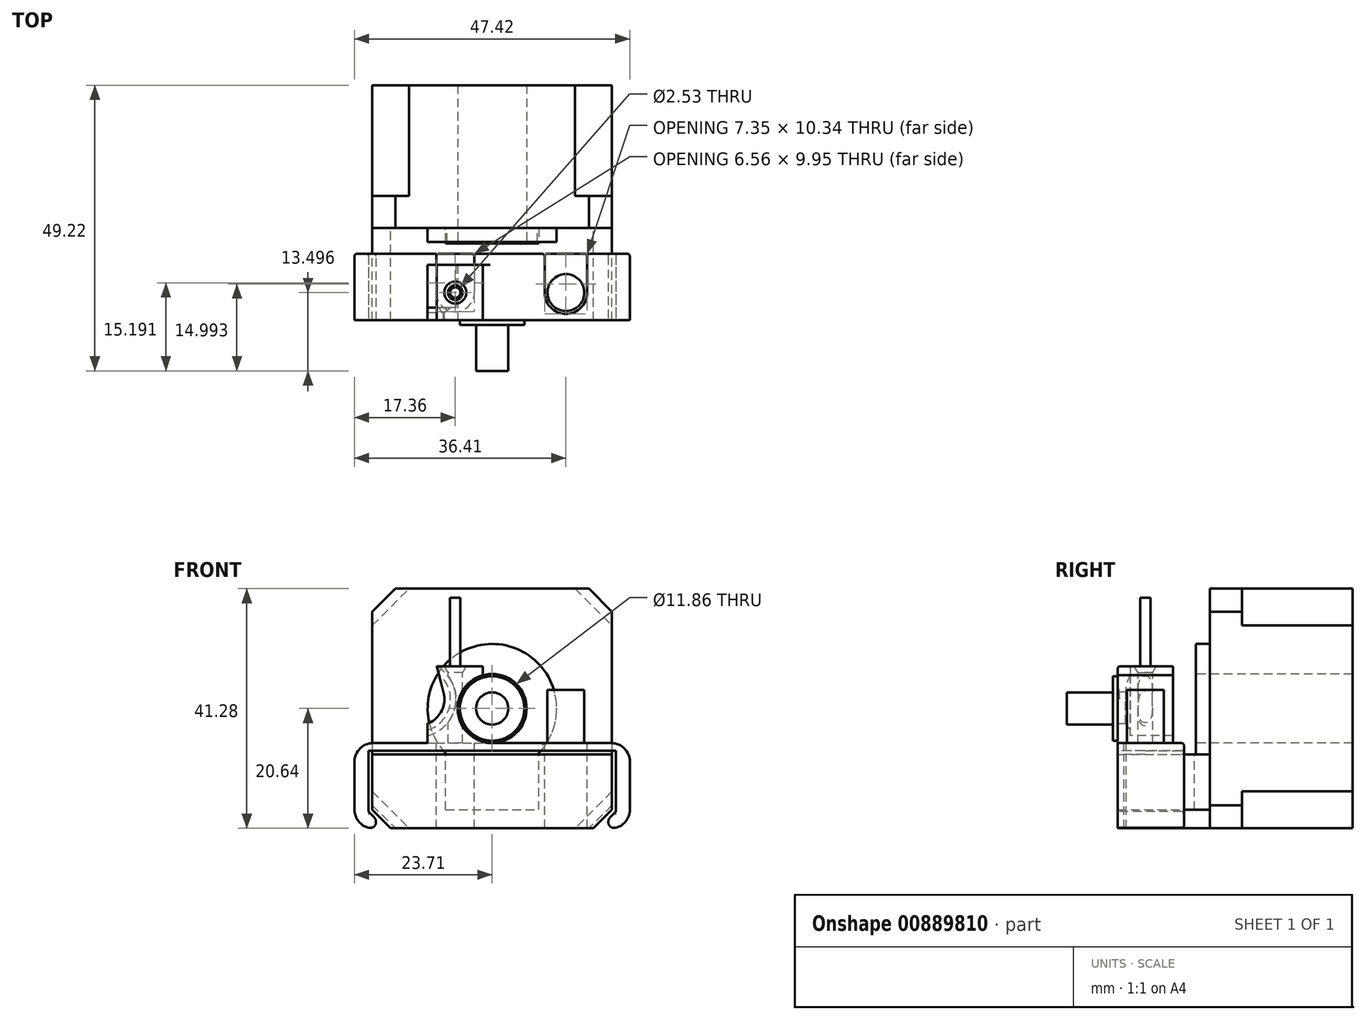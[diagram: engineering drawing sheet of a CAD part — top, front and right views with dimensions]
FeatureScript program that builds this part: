
annotation { "Feature Type Name" : "Feature", "Feature Type Description" : "" }
export const myFeature = defineFeature(function(context is Context, id is Id, definition is map)
    precondition{}
    {
        {
            var Q0;
            Q0=qCreatedBy(makeId("Front.planeOp"),FACE);
            var sketch = newSketch(context, id + "F0", { "sketchPlane" : qUnion([Q0])});
            skLineSegment(sketch, "E0.bottom", {"start": v(14.29, 20.64) * mm, "end": v(-14.29, 20.64) * mm});
            skLineSegment(sketch, "E0.top", {"start": v(14.29, -20.64) * mm, "end": v(-14.29, -20.64) * mm});
            skLineSegment(sketch, "E0.left", {"start": v(20.64, 14.29) * mm, "end": v(20.64, -14.29) * mm});
            skLineSegment(sketch, "E0.right", {"start": v(-20.64, 14.29) * mm, "end": v(-20.64, -14.29) * mm});
            skPoint(sketch, "E0.middle", {"position": v(0, 0) * mm});
            skLineSegment(sketch, "E1", {"start": v(-20.64, 14.29) * mm, "end": v(-14.29, 20.64) * mm});
            skLineSegment(sketch, "E2", {"start": v(14.29, 20.64) * mm, "end": v(20.64, 14.29) * mm});
            skLineSegment(sketch, "E3", {"start": v(20.64, -14.29) * mm, "end": v(14.29, -20.64) * mm});
            skLineSegment(sketch, "E4", {"start": v(-20.64, -14.29) * mm, "end": v(-14.29, -20.64) * mm});
            skPoint(sketch, "E5.orphan", {"position": v(20.64, -20.64) * mm});
            skPoint(sketch, "E6.orphan", {"position": v(20.64, 20.64) * mm});
            skPoint(sketch, "E7.orphan", {"position": v(-20.64, 20.64) * mm});
            skPoint(sketch, "E8.orphan", {"position": v(-20.64, -20.64) * mm});
            skSolve(sketch);
        }
        {
            var Q0;
            Q0=makeQuery(id+"F0.imprint","IMPRINT",FACE,{"disambiguationData":[TD([[makeQuery(id+"F0.imprint","IMPRINT",EDGE,{"derivedFrom":sQuery(id+"F0.wireOp",EDGE,"E0.bottom")}),1.0]])]});
            extrude(context, id + "F1", {"entities" : qUnion([Q0]), "endBound" : BoundingType.SYMMETRIC, "depth" : 19.05 * mm, "offsetDistance" : 25.4 * mm});
        }
        {
            var Q0;
            Q0=makeQuery(id+"F1.opExtrude","CAP_FACE",FACE,{"disambiguationData":[OSD([sQuery(id+"F0.wireOp",EDGE,"E0.bottom"),sQuery(id+"F0.wireOp",EDGE,"E0.top"),sQuery(id+"F0.wireOp",EDGE,"E0.left"),sQuery(id+"F0.wireOp",EDGE,"E0.right"),sQuery(id+"F0.wireOp",EDGE,"E1"),sQuery(id+"F0.wireOp",EDGE,"E2"),sQuery(id+"F0.wireOp",EDGE,"E3"),sQuery(id+"F0.wireOp",EDGE,"E4")])],"isStart":false});
            var sketch = newSketch(context, id + "F2", { "sketchPlane" : qUnion([Q0])});
            skLineSegment(sketch, "E9.bottom", {"start": v(-20.64, 20.64) * mm, "end": v(20.64, 20.64) * mm});
            skLineSegment(sketch, "E9.top", {"start": v(-20.64, -20.64) * mm, "end": v(20.64, -20.64) * mm});
            skLineSegment(sketch, "E9.left", {"start": v(-20.64, 20.64) * mm, "end": v(-20.64, -20.64) * mm});
            skLineSegment(sketch, "E9.right", {"start": v(20.64, 20.64) * mm, "end": v(20.64, -20.64) * mm});
            skPoint(sketch, "E9.middle", {"position": v(0, 0) * mm});
            skLineSegment(sketch, "E10", {"start": v(-20.64, 16.67) * mm, "end": v(-16.67, 20.64) * mm});
            skLineSegment(sketch, "E11", {"start": v(16.67, 20.64) * mm, "end": v(20.64, 16.67) * mm});
            skLineSegment(sketch, "E12", {"start": v(20.64, -16.67) * mm, "end": v(16.67, -20.64) * mm});
            skLineSegment(sketch, "E13", {"start": v(-20.64, -16.67) * mm, "end": v(-16.67, -20.64) * mm});
            skSolve(sketch);
        }
        {
            var Q0;
            {var subQ2=sQuery(id+"F2.wireOp",EDGE,"E10");Q0=makeQuery(id+"F2.imprint","IMPRINT",FACE,{"disambiguationData":[TD([[makeQuery(id+"F2.imprint","IMPRINT",EDGE,{"derivedFrom":subQ2}),-1.0]])]});}
            var Q1;
            {var subQ4=makeQuery(id+"F1.opExtrude","CAP_EDGE",EDGE,{"disambiguationData":[OSD([sQuery(id+"F0.wireOp",EDGE,"E1")])],"isStart":false});Q1=makeQuery(id+"F2.imprint","IMPRINT",FACE,{"disambiguationData":[TD([[makeQuery(id+"F2.imprint","IMPRINT",EDGE,{"derivedFrom":subQ4}),-1.0]])]});}
            var Q2;
            {var subQ2=sQuery(id+"F2.wireOp",EDGE,"E13");Q2=makeQuery(id+"F2.imprint","IMPRINT",FACE,{"disambiguationData":[TD([[makeQuery(id+"F2.imprint","IMPRINT",EDGE,{"derivedFrom":subQ2}),1.0]])]});}
            var Q3;
            {var subQ2=sQuery(id+"F2.wireOp",EDGE,"E12");Q3=makeQuery(id+"F2.imprint","IMPRINT",FACE,{"disambiguationData":[TD([[makeQuery(id+"F2.imprint","IMPRINT",EDGE,{"derivedFrom":subQ2}),-1.0]])]});}
            var Q4;
            {var subQ2=sQuery(id+"F2.wireOp",EDGE,"E11");Q4=makeQuery(id+"F2.imprint","IMPRINT",FACE,{"disambiguationData":[TD([[makeQuery(id+"F2.imprint","IMPRINT",EDGE,{"derivedFrom":subQ2}),-1.0]])]});}
            extrude(context, id + "F3", {"entities" : qUnion([Q0, Q1, Q2, Q3, Q4]), "operationType" : NewBodyOperationType.ADD, "depth" : 5.56 * mm, "offsetDistance" : 25.4 * mm});
        }
        {
            var Q0;
            Q0=makeQuery(id+"F3.opExtrude","CAP_FACE",FACE,{"disambiguationData":[OSD([sQuery(id+"F2.wireOp",EDGE,"E9.bottom"),sQuery(id+"F2.wireOp",EDGE,"E9.top"),sQuery(id+"F2.wireOp",EDGE,"E9.left"),sQuery(id+"F2.wireOp",EDGE,"E9.right"),sQuery(id+"F2.wireOp",EDGE,"E10"),sQuery(id+"F2.wireOp",EDGE,"E11"),sQuery(id+"F2.wireOp",EDGE,"E12"),sQuery(id+"F2.wireOp",EDGE,"E13")])],"isStart":false});
            var sketch = newSketch(context, id + "F4", { "sketchPlane" : qUnion([Q0])});
            skCircle(sketch, "E14", {"center": v(0, 0) * mm, "radius": 11.11 * mm});
            skSolve(sketch);
        }
        {
            var Q0;
            Q0=makeQuery(id+"F4.imprint","IMPRINT",FACE,{"disambiguationData":[TD([[makeQuery(id+"F4.imprint","IMPRINT",EDGE,{"derivedFrom":sQuery(id+"F4.wireOp",EDGE,"E14")}),1.0]])]});
            extrude(context, id + "F5", {"entities" : qUnion([Q0]), "operationType" : NewBodyOperationType.ADD, "depth" : 2.38 * mm, "offsetDistance" : 25.4 * mm});
        }
        {
            var Q0;
            Q0=makeQuery(id+"F5.opExtrude","CAP_FACE",FACE,{"disambiguationData":[OSD([sQuery(id+"F4.wireOp",EDGE,"E14")])],"isStart":false});
            var sketch = newSketch(context, id + "F6", { "sketchPlane" : qUnion([Q0])});
            skCircle(sketch, "E15", {"center": v(0, 0) * mm, "radius": 2.78 * mm});
            skSolve(sketch);
        }
        {
            var Q0;
            Q0=makeQuery(id+"F6.imprint","IMPRINT",FACE,{"disambiguationData":[TD([[makeQuery(id+"F6.imprint","IMPRINT",EDGE,{"derivedFrom":sQuery(id+"F6.wireOp",EDGE,"E15")}),1.0]])]});
            extrude(context, id + "F7", {"entities" : qUnion([Q0]), "operationType" : NewBodyOperationType.ADD, "depth" : 22.22 * mm, "offsetDistance" : 25.4 * mm});
        }
        {
            var Q0;
            Q0=makeQuery(id+"F5.opExtrude","CAP_FACE",FACE,{"disambiguationData":[OSD([sQuery(id+"F4.wireOp",EDGE,"E14")])],"isStart":false});
            cPlane(context, id + "F8", {"entities" : qUnion([Q0]), "cplaneType" : CPlaneType.OFFSET, "offset" : 4.76 * mm, "width" : 152.4 * mm, "height" : 152.4 * mm});
        }
        {
            var Q0;
            Q0=qCreatedBy(id+"F8.planeOp",FACE);
            var sketch = newSketch(context, id + "F9", { "sketchPlane" : qUnion([Q0])});
            skCircle(sketch, "E16", {"center": v(0, 0) * mm, "radius": 5.56 * mm});
            skSolve(sketch);
        }
        {
            var Q0;
            Q0=makeQuery(id+"F9.imprint","IMPRINT",FACE,{"disambiguationData":[TD([[makeQuery(id+"F9.imprint","IMPRINT",EDGE,{"derivedFrom":sQuery(id+"F9.wireOp",EDGE,"E16")}),1.0]])]});
            extrude(context, id + "F10", {"entities" : qUnion([Q0]), "operationType" : NewBodyOperationType.ADD, "depth" : 9.52 * mm, "offsetDistance" : 25.4 * mm});
        }
        {
            var Q0;
            Q0=makeQuery(id+"F3.opExtrude","CAP_FACE",FACE,{"disambiguationData":[OSD([sQuery(id+"F2.wireOp",EDGE,"E9.bottom"),sQuery(id+"F2.wireOp",EDGE,"E9.top"),sQuery(id+"F2.wireOp",EDGE,"E9.left"),sQuery(id+"F2.wireOp",EDGE,"E9.right"),sQuery(id+"F2.wireOp",EDGE,"E10"),sQuery(id+"F2.wireOp",EDGE,"E11"),sQuery(id+"F2.wireOp",EDGE,"E12"),sQuery(id+"F2.wireOp",EDGE,"E13")])],"isStart":false});
            var sketch = newSketch(context, id + "F11", { "sketchPlane" : qUnion([Q0])});
            skLineSegment(sketch, "E17.bottom", {"start": v(-17.46, -20.64) * mm, "end": v(17.46, -20.64) * mm});
            skLineSegment(sketch, "E17.top", {"start": v(-20.64, -7.94) * mm, "end": v(20.64, -7.94) * mm});
            skLineSegment(sketch, "E17.left", {"start": v(-20.64, -17.46) * mm, "end": v(-20.64, -7.94) * mm});
            skLineSegment(sketch, "E17.right", {"start": v(20.64, -17.46) * mm, "end": v(20.64, -7.94) * mm});
            skLineSegment(sketch, "E18", {"start": v(-20.64, -17.46) * mm, "end": v(-17.46, -20.64) * mm});
            skLineSegment(sketch, "E19", {"start": v(17.46, -20.64) * mm, "end": v(20.64, -17.46) * mm});
            skPoint(sketch, "E20.orphan", {"position": v(-20.64, -20.64) * mm});
            skSolve(sketch);
        }
        {
            var Q0;
            Q0 = qSketchRegion(id + "F11", true);
            extrude(context, id + "F12", {"entities" : qUnion([Q0]), "depth" : 15.88 * mm, "offsetDistance" : 25.4 * mm});
        }
        {
            var Q0;
            Q0=makeQuery(id+"F12.opExtrude","SWEPT_FACE",FACE,{"disambiguationData":[OSD([sQuery(id+"F11.wireOp",EDGE,"E17.top")])]});
            var sketch = newSketch(context, id + "F13", { "sketchPlane" : qUnion([Q0])});
            skLineSegment(sketch, "E21", {"start": v(-7.78, -17.46) * mm, "end": v(-7.78, -15.08) * mm});
            skLineSegment(sketch, "E22", {"start": v(7.78, -15.08) * mm, "end": v(7.78, -17.46) * mm});
            skLineSegment(sketch, "E23", {"start": v(-7.78, -17.46) * mm, "end": v(7.78, -17.46) * mm});
            skLineSegment(sketch, "E24.0", {"start": v(-8.03, -17.71) * mm, "end": v(-8.03, -15.08) * mm});
            skLineSegment(sketch, "E24.1", {"start": v(-8.03, -17.71) * mm, "end": v(8.03, -17.71) * mm});
            skLineSegment(sketch, "E24.2", {"start": v(8.03, -15.08) * mm, "end": v(8.03, -17.71) * mm});
            skLineSegment(sketch, "E25", {"start": v(-8.03, -15.08) * mm, "end": v(8.03, -15.08) * mm});
            skSolve(sketch);
        }
        {
            var Q0;
            {var subQ0=sQuery(id+"F13.wireOp",EDGE,"E21");Q0=makeQuery(id+"F13.imprint","IMPRINT",FACE,{"disambiguationData":[TD([[makeQuery(id+"F13.imprint","IMPRINT",EDGE,{"derivedFrom":subQ0}),-1.0]])]});}
            var Q1;
            {var subQ2=sQuery(id+"F13.wireOp",EDGE,"E21");Q1=makeQuery(id+"F13.imprint","IMPRINT",FACE,{"disambiguationData":[TD([[makeQuery(id+"F13.imprint","IMPRINT",EDGE,{"derivedFrom":subQ2}),1.0]])]});}
            extrude(context, id + "F14", {"entities" : qUnion([Q0, Q1]), "operationType" : NewBodyOperationType.REMOVE, "oppositeDirection" : true, "depth" : 9.52 * mm, "offsetDistance" : 25.4 * mm});
        }
        {
            var Q0;
            Q0=makeQuery(id+"F12.opExtrude","SWEPT_FACE",FACE,{"disambiguationData":[OSD([sQuery(id+"F11.wireOp",EDGE,"E17.top")])]});
            var sketch = newSketch(context, id + "F15", { "sketchPlane" : qUnion([Q0])});
            skCircle(sketch, "E26", {"center": v(-6.35, -26.2) * mm, "radius": 2.78 * mm});
            skSolve(sketch);
        }
        {
            var Q0;
            Q0=makeQuery(id+"F15.imprint","IMPRINT",FACE,{"disambiguationData":[TD([[makeQuery(id+"F15.imprint","IMPRINT",EDGE,{"derivedFrom":sQuery(id+"F15.wireOp",EDGE,"E26")}),1.0]])]});
            extrude(context, id + "F16", {"entities" : qUnion([Q0]), "operationType" : NewBodyOperationType.ADD, "depth" : 1.59 * mm, "offsetDistance" : 25.4 * mm});
        }
        {
            var Q0;
            Q0=makeQuery(id+"F12.opExtrude","SWEPT_FACE",FACE,{"disambiguationData":[OSD([sQuery(id+"F11.wireOp",EDGE,"E17.top")])]});
            var sketch = newSketch(context, id + "F17", { "sketchPlane" : qUnion([Q0])});
            skCircle(sketch, "E27", {"center": v(12.7, -26.2) * mm, "radius": 3.18 * mm});
            skSolve(sketch);
        }
        {
            var Q0;
            Q0=makeQuery(id+"F17.imprint","IMPRINT",FACE,{"disambiguationData":[TD([[makeQuery(id+"F17.imprint","IMPRINT",EDGE,{"derivedFrom":sQuery(id+"F17.wireOp",EDGE,"E27")}),1.0]])]});
            extrude(context, id + "F18", {"entities" : qUnion([Q0]), "operationType" : NewBodyOperationType.ADD, "depth" : 11.1 * mm, "offsetDistance" : 25.4 * mm});
        }
        {
            var Q0;
            Q0=makeQuery(id+"F16.opExtrude","CAP_FACE",FACE,{"disambiguationData":[OSD([sQuery(id+"F15.wireOp",EDGE,"E26")])],"isStart":false});
            var sketch = newSketch(context, id + "F19", { "sketchPlane" : qUnion([Q0])});
            skCircle(sketch, "E28", {"center": v(-6.35, -26.2) * mm, "radius": 0.89 * mm});
            skSolve(sketch);
        }
        {
            var Q0;
            Q0=makeQuery(id+"F19.imprint","IMPRINT",FACE,{"disambiguationData":[TD([[makeQuery(id+"F19.imprint","IMPRINT",EDGE,{"derivedFrom":sQuery(id+"F19.wireOp",EDGE,"E28")}),1.0]])]});
            extrude(context, id + "F20", {"entities" : qUnion([Q0]), "depth" : 25.4 * mm, "offsetDistance" : 25.4 * mm});
        }
        {
            var Q0;
            Q0=makeQuery(id+"F20.opExtrude","CAP_FACE",FACE,{"disambiguationData":[OSD([sQuery(id+"F19.wireOp",EDGE,"E28")])],"isStart":false});
            var sketch = newSketch(context, id + "F21", { "sketchPlane" : qUnion([Q0])});
            skPoint(sketch, "E29", {"position": v(-6.35, -26.2) * mm});
            skSolve(sketch);
        }
        {
            var Q0;
            Q0=sQuery(id+"F21.wireOp",VERTEX,"E29");
            var Q1;
            Q1=qCreatedBy(makeId("Front.planeOp"),FACE);
            cPlane(context, id + "F22", {"entities" : qUnion([Q0, Q1]), "cplaneType" : CPlaneType.PLANE_POINT, "offset" : 25.4 * mm, "width" : 152.4 * mm, "height" : 152.4 * mm});
        }
        {
            var Q0;
            Q0=qCreatedBy(id+"F22.planeOp",FACE);
            var sketch = newSketch(context, id + "F23", { "sketchPlane" : qUnion([Q0])});
            skCircle(sketch, "E30", {"center": v(-12.7, 1.59) * mm, "radius": 6.1 * mm});
            skSolve(sketch);
        }
        {
            var Q0;
            Q0=makeQuery(id+"F23.imprint","IMPRINT",FACE,{"disambiguationData":[TD([[makeQuery(id+"F23.imprint","IMPRINT",EDGE,{"derivedFrom":sQuery(id+"F23.wireOp",EDGE,"E30")}),1.0]])]});
            extrude(context, id + "F24", {"entities" : qUnion([Q0]), "endBound" : BoundingType.SYMMETRIC, "depth" : 3.17 * mm, "offsetDistance" : 25.4 * mm});
        }
        {
            var Q0;
            Q0=makeQuery(id+"F12.opExtrude","CAP_FACE",FACE,{"disambiguationData":[OSD([sQuery(id+"F11.wireOp",EDGE,"E17.bottom"),sQuery(id+"F11.wireOp",EDGE,"E17.top"),sQuery(id+"F11.wireOp",EDGE,"E17.left"),sQuery(id+"F11.wireOp",EDGE,"E17.right"),sQuery(id+"F11.wireOp",EDGE,"E18"),sQuery(id+"F11.wireOp",EDGE,"E19")])],"isStart":false});
            var sketch = newSketch(context, id + "F25", { "sketchPlane" : qUnion([Q0])});
            skLineSegment(sketch, "E31.0", {"start": v(21.33, -7.25) * mm, "end": v(-21.33, -7.25) * mm});
            skLineSegment(sketch, "E31.1", {"start": v(-21.33, -17.75) * mm, "end": v(-17.75, -21.33) * mm});
            skLineSegment(sketch, "E31.2", {"start": v(-17.75, -21.33) * mm, "end": v(17.75, -21.33) * mm});
            skLineSegment(sketch, "E31.3", {"start": v(-21.33, -7.25) * mm, "end": v(-21.33, -17.75) * mm});
            skLineSegment(sketch, "E31.4", {"start": v(17.75, -21.33) * mm, "end": v(21.33, -17.75) * mm});
            skLineSegment(sketch, "E31.5", {"start": v(21.33, -17.75) * mm, "end": v(21.33, -7.25) * mm});
            skLineSegment(sketch, "E32.bottom", {"start": v(-23.7, -20.64) * mm, "end": v(23.7, -20.64) * mm});
            skLineSegment(sketch, "E32.top", {"start": v(-23.7, -5.98) * mm, "end": v(23.7, -5.98) * mm});
            skLineSegment(sketch, "E32.left", {"start": v(-23.7, -20.64) * mm, "end": v(-23.7, -5.98) * mm});
            skLineSegment(sketch, "E32.right", {"start": v(23.7, -20.64) * mm, "end": v(23.7, -5.98) * mm});
            skPoint(sketch, "E32.middle", {"position": v(0, -13.3) * mm});
            skPoint(sketch, "E32.middle.positionSnap0", {"position": v(0, -20.64) * mm});
            skPoint(sketch, "E32.centerSnap0", {"position": v(0, -20.64) * mm});
            skLineSegment(sketch, "E33.0", {"start": v(-9.13, -6.35) * mm, "end": v(-3.57, -6.35) * mm, "construction": true});
            skSolve(sketch);
        }
        {
            var Q0;
            Q0=makeQuery(id+"F25.imprint","IMPRINT",FACE,{"disambiguationData":[TD([[makeQuery(id+"F25.imprint","IMPRINT",EDGE,{"derivedFrom":sQuery(id+"F25.wireOp",EDGE,"E31.0")}),-1.0]])]});
            var Q1;
            Q1=makeQuery(id+"F10.opExtrude","CAP_FACE",FACE,{"disambiguationData":[OSD([sQuery(id+"F9.wireOp",EDGE,"E16")])],"isStart":true});
            extrude(context, id + "F26", {"entities" : qUnion([Q0]), "oppositeDirection" : true, "depth" : 11.43 * mm, "endBoundEntityFace" : qUnion([Q1]), "offsetDistance" : 25.4 * mm});
        }
        {
            var Q0;
            Q0=makeQuery(id+"F26.opExtrude","SWEPT_FACE",FACE,{"disambiguationData":[OSD([sQuery(id+"F25.wireOp",EDGE,"E32.top")])]});
            var sketch = newSketch(context, id + "F27", { "sketchPlane" : qUnion([Q0])});
            skArc(sketch, "E34.0", {"start": v(-9.63, -26.2) * mm, "mid": v(-6.35, -29.47) * mm, "end": v(-3.07, -26.2) * mm});
            skArc(sketch, "E35.0", {"start": v(9.03, -26.2) * mm, "mid": v(12.7, -29.87) * mm, "end": v(16.38, -26.2) * mm});
            skCircle(sketch, "E36", {"center": v(12.7, -26.2) * mm, "radius": 3.18 * mm, "construction": true});
            skLineSegment(sketch, "E37", {"start": v(15.34, -27.95) * mm, "end": v(15.76, -28.23) * mm, "construction": true});
            skLineSegment(sketch, "E38", {"start": v(-8.09, -28.97) * mm, "end": v(-7.82, -28.55) * mm, "construction": true});
            skLineSegment(sketch, "E39", {"start": v(-9.63, -26.2) * mm, "end": v(-9.63, -19.53) * mm});
            skLineSegment(sketch, "E40", {"start": v(-3.07, -19.53) * mm, "end": v(-3.07, -26.2) * mm});
            skLineSegment(sketch, "E41", {"start": v(-9.63, -19.53) * mm, "end": v(-3.07, -19.53) * mm});
            skLineSegment(sketch, "E42", {"start": v(9.03, -26.2) * mm, "end": v(9.03, -19.53) * mm});
            skLineSegment(sketch, "E43", {"start": v(9.03, -19.53) * mm, "end": v(16.38, -19.53) * mm});
            skLineSegment(sketch, "E44", {"start": v(16.38, -19.53) * mm, "end": v(16.38, -26.2) * mm});
            skSolve(sketch);
        }
        {
            var Q0;
            Q0=makeQuery(id+"F27.imprint","IMPRINT",FACE,{"disambiguationData":[TD([[makeQuery(id+"F27.imprint","IMPRINT",EDGE,{"derivedFrom":sQuery(id+"F27.wireOp",EDGE,"E34.0")}),1.0]])]});
            var Q1;
            Q1=makeQuery(id+"F27.imprint","IMPRINT",FACE,{"disambiguationData":[TD([[makeQuery(id+"F27.imprint","IMPRINT",EDGE,{"derivedFrom":sQuery(id+"F27.wireOp",EDGE,"E35.0")}),1.0]])]});
            extrude(context, id + "F28", {"entities" : qUnion([Q0, Q1]), "operationType" : NewBodyOperationType.REMOVE, "endBound" : BoundingType.THROUGH_ALL, "oppositeDirection" : true, "depth" : 25.4 * mm, "offsetDistance" : 25.4 * mm});
        }
        {
            var Q0;
            Q0=makeQuery(id+"F26.opExtrude","SWEPT_FACE",FACE,{"disambiguationData":[OSD([sQuery(id+"F25.wireOp",EDGE,"E32.top")])]});
            var sketch = newSketch(context, id + "F29", { "sketchPlane" : qUnion([Q0])});
            skLineSegment(sketch, "E45.bottom", {"start": v(-11.11, -30.96) * mm, "end": v(-1.59, -30.96) * mm});
            skLineSegment(sketch, "E45.top", {"start": v(-11.11, -21.43) * mm, "end": v(-1.59, -21.43) * mm});
            skLineSegment(sketch, "E45.left", {"start": v(-11.11, -30.96) * mm, "end": v(-11.11, -21.43) * mm});
            skLineSegment(sketch, "E45.right", {"start": v(-1.59, -30.96) * mm, "end": v(-1.59, -21.43) * mm});
            skPoint(sketch, "E45.middle", {"position": v(-6.35, -26.2) * mm});
            skSolve(sketch);
        }
        {
            var Q0;
            Q0 = qSketchRegion(id + "F29", true);
            extrude(context, id + "F30", {"entities" : qUnion([Q0]), "operationType" : NewBodyOperationType.ADD, "depth" : 13.2 * mm, "offsetDistance" : 25.4 * mm});
        }
        {
            var Q0;
            Q0=makeQuery(id+"F24.opExtrude","CAP_FACE",FACE,{"disambiguationData":[OSD([sQuery(id+"F23.wireOp",EDGE,"E30")])],"isStart":false});
            cPlane(context, id + "F31", {"entities" : qUnion([Q0]), "cplaneType" : CPlaneType.OFFSET, "offset" : 1 * mm, "width" : 152.4 * mm, "height" : 152.4 * mm});
        }
        {
            var Q0;
            Q0=qCreatedBy(id+"F31.planeOp",FACE);
            var sketch = newSketch(context, id + "F32", { "sketchPlane" : qUnion([Q0])});
            skCircle(sketch, "E46.0", {"center": v(-12.7, 1.59) * mm, "radius": 6.47 * mm});
            skSolve(sketch);
        }
        {
            var Q0;
            Q0=makeQuery(id+"F32.imprint","IMPRINT",FACE,{"disambiguationData":[TD([[makeQuery(id+"F32.imprint","IMPRINT",EDGE,{"derivedFrom":sQuery(id+"F32.wireOp",EDGE,"E46.0")}),1.0]])]});
            var Q1;
            {var subQ0=sQuery(id+"F25.wireOp",EDGE,"E32.left");var subQ1=sQuery(id+"F25.wireOp",EDGE,"E32.bottom");var subQ2=sQuery(id+"F25.wireOp",EDGE,"E31.1");var subQ3=sQuery(id+"F25.wireOp",EDGE,"E31.3");var subQ4=sQuery(id+"F25.wireOp",EDGE,"E31.0");var subQ5=sQuery(id+"F25.wireOp",EDGE,"E32.top");Q1=makeQuery(id+"F28.boolean.opBoolean","SPLIT",FACE,{"disambiguationData":[TD([makeQuery(id+"F26.opExtrude","SWEPT_FACE",FACE,{"disambiguationData":[OSD([subQ2])]})])],"derivedFrom":makeQuery(id+"F26.opExtrude","CAP_FACE",FACE,{"disambiguationData":[OSD([subQ4,subQ2,subQ3,sQuery(id+"F25.wireOp",EDGE,"E31.4"),sQuery(id+"F25.wireOp",EDGE,"E31.5"),subQ1,subQ5,subQ0,sQuery(id+"F25.wireOp",EDGE,"E32.right")])],"isStart":false})});}
            extrude(context, id + "F33", {"entities" : qUnion([Q0]), "operationType" : NewBodyOperationType.REMOVE, "endBound" : BoundingType.UP_TO_SURFACE, "oppositeDirection" : true, "depth" : 25.4 * mm, "endBoundEntityFace" : qUnion([Q1]), "offsetDistance" : 25.4 * mm});
        }
        {
            var Q0;
            Q0=makeQuery(id+"F30.boolean.opBoolean","MERGE",FACE,{"derivedFrom":[makeQuery(id+"F26.opExtrude","CAP_FACE",FACE,{"disambiguationData":[OSD([sQuery(id+"F25.wireOp",EDGE,"E31.0"),sQuery(id+"F25.wireOp",EDGE,"E31.1"),sQuery(id+"F25.wireOp",EDGE,"E31.3"),sQuery(id+"F25.wireOp",EDGE,"E31.4"),sQuery(id+"F25.wireOp",EDGE,"E31.5"),sQuery(id+"F25.wireOp",EDGE,"E32.bottom"),sQuery(id+"F25.wireOp",EDGE,"E32.top"),sQuery(id+"F25.wireOp",EDGE,"E32.left"),sQuery(id+"F25.wireOp",EDGE,"E32.right")])],"isStart":true}),makeQuery(id+"F30.opExtrude","SWEPT_FACE",FACE,{"disambiguationData":[OSD([sQuery(id+"F29.wireOp",EDGE,"E45.bottom")])]})]});
            var sketch = newSketch(context, id + "F34", { "sketchPlane" : qUnion([Q0])});
            skCircle(sketch, "E47.0", {"center": v(0, 0) * mm, "radius": 5.93 * mm});
            skSolve(sketch);
        }
        {
            var Q0;
            Q0 = qSketchRegion(id + "F34", true);
            extrude(context, id + "F35", {"entities" : qUnion([Q0]), "operationType" : NewBodyOperationType.REMOVE, "endBound" : BoundingType.THROUGH_ALL, "oppositeDirection" : true, "depth" : 25.4 * mm, "offsetDistance" : 25.4 * mm});
        }
        {
            var Q0;
            Q0=makeQuery(id+"F30.opExtrude","CAP_FACE",FACE,{"disambiguationData":[OSD([sQuery(id+"F29.wireOp",EDGE,"E45.bottom"),sQuery(id+"F29.wireOp",EDGE,"E45.top"),sQuery(id+"F29.wireOp",EDGE,"E45.left"),sQuery(id+"F29.wireOp",EDGE,"E45.right")])],"isStart":false});
            var sketch = newSketch(context, id + "F36", { "sketchPlane" : qUnion([Q0])});
            skCircle(sketch, "E48.0", {"center": v(-6.35, -26.2) * mm, "radius": 1.26 * mm});
            skSolve(sketch);
        }
        {
            var Q0;
            Q0 = qSketchRegion(id + "F36", true);
            extrude(context, id + "F37", {"entities" : qUnion([Q0]), "operationType" : NewBodyOperationType.REMOVE, "endBound" : BoundingType.THROUGH_ALL, "oppositeDirection" : true, "depth" : 25.4 * mm, "offsetDistance" : 25.4 * mm});
        }
        {
            var Q0;
            Q0=makeQuery(id+"F30.opExtrude","CAP_EDGE",EDGE,{"disambiguationData":[OSD([sQuery(id+"F29.wireOp",EDGE,"E45.left")])],"isStart":true});
            var Q1;
            Q1=makeQuery(id+"F30.opExtrude","CAP_EDGE",EDGE,{"disambiguationData":[OSD([sQuery(id+"F29.wireOp",EDGE,"E45.right")])],"isStart":true});
            var Q2;
            Q2=makeQuery(id+"F26.opExtrude","SWEPT_EDGE",EDGE,{"disambiguationData":[OSD([sQuery(id+"F25.wireOp",EDGE,"E32.top"),sQuery(id+"F25.wireOp",EDGE,"E32.left")])]});
            var Q3;
            Q3=makeQuery(id+"F26.opExtrude","SWEPT_EDGE",EDGE,{"disambiguationData":[OSD([sQuery(id+"F25.wireOp",EDGE,"E32.bottom"),sQuery(id+"F25.wireOp",EDGE,"E32.left")])]});
            var Q4;
            Q4=makeQuery(id+"F26.opExtrude","SWEPT_EDGE",EDGE,{"disambiguationData":[OSD([sQuery(id+"F25.wireOp",EDGE,"E32.top"),sQuery(id+"F25.wireOp",EDGE,"E32.right")])]});
            var Q5;
            Q5=makeQuery(id+"F26.opExtrude","SWEPT_EDGE",EDGE,{"disambiguationData":[OSD([sQuery(id+"F25.wireOp",EDGE,"E32.bottom"),sQuery(id+"F25.wireOp",EDGE,"E32.right")])]});
            fillet(context, id + "F38", {"entities" : qUnion([Q0, Q1, Q2, Q3, Q4, Q5]), "radius" : 3.17 * mm, "tangentPropagation" : true, "allowEdgeOverflow" : false});
        }
        {
            var Q0;
            Q0=makeQuery(id+"F38.opFillet","BLEND_EDGE",EDGE,{"blendedFrom":[makeQuery(id+"F30.opExtrude","CAP_EDGE",EDGE,{"disambiguationData":[OSD([sQuery(id+"F29.wireOp",EDGE,"E45.left")])],"isStart":true}),makeQuery(id+"F33.boolean.opBoolean","COPY",FACE,{"derivedFrom":makeQuery(id+"F33.opExtrude","SWEPT_FACE",FACE,{"disambiguationData":[OSD([sQuery(id+"F32.wireOp",EDGE,"E46.0")])]})})],"blendedInto":[makeQuery(id+"F33.boolean.opBoolean","COPY",FACE,{"derivedFrom":makeQuery(id+"F33.opExtrude","SWEPT_FACE",FACE,{"disambiguationData":[OSD([sQuery(id+"F32.wireOp",EDGE,"E46.0")])]})})]});
            var Q1;
            Q1=makeQuery(id+"F38.opFillet","BLEND_EDGE",EDGE,{"blendedFrom":[makeQuery(id+"F30.opExtrude","CAP_EDGE",EDGE,{"disambiguationData":[OSD([sQuery(id+"F29.wireOp",EDGE,"E45.right")])],"isStart":true}),makeQuery(id+"F35.boolean.opBoolean","COPY",FACE,{"derivedFrom":makeQuery(id+"F35.opExtrude","SWEPT_FACE",FACE,{"disambiguationData":[OSD([sQuery(id+"F34.wireOp",EDGE,"E47.0")])]})})],"blendedInto":[makeQuery(id+"F35.boolean.opBoolean","COPY",FACE,{"derivedFrom":makeQuery(id+"F35.opExtrude","SWEPT_FACE",FACE,{"disambiguationData":[OSD([sQuery(id+"F34.wireOp",EDGE,"E47.0")])]})})]});
            var Q2;
            Q2=makeQuery(id+"F26.opExtrude","SWEPT_EDGE",EDGE,{"disambiguationData":[OSD([sQuery(id+"F25.wireOp",EDGE,"E31.1"),sQuery(id+"F25.wireOp",EDGE,"E32.bottom")])]});
            var Q3;
            Q3=makeQuery(id+"F26.opExtrude","SWEPT_EDGE",EDGE,{"disambiguationData":[OSD([sQuery(id+"F25.wireOp",EDGE,"E31.4"),sQuery(id+"F25.wireOp",EDGE,"E32.bottom")])]});
            fillet(context, id + "F39", {"entities" : qUnion([Q0, Q1, Q2, Q3]), "radius" : 1.27 * mm, "tangentPropagation" : true, "allowEdgeOverflow" : false});
        }
        {
            var Q0;
            {var subQ0=sQuery(id+"F25.wireOp",EDGE,"E32.bottom");Q0=makeQuery(id+"F39.opFillet","BLEND_EDGE",EDGE,{"blendedFrom":[makeQuery(id+"F26.opExtrude","SWEPT_EDGE",EDGE,{"disambiguationData":[OSD([sQuery(id+"F25.wireOp",EDGE,"E31.1"),subQ0])]}),makeQuery(id+"F38.opFillet","BLEND_FACE",FACE,{"disambiguationData":[OSD([subQ0,sQuery(id+"F25.wireOp",EDGE,"E32.left")])]})],"blendedInto":[makeQuery(id+"F38.opFillet","BLEND_FACE",FACE,{"disambiguationData":[OSD([subQ0,sQuery(id+"F25.wireOp",EDGE,"E32.left")])]})]});}
            var Q1;
            {var subQ0=sQuery(id+"F25.wireOp",EDGE,"E32.bottom");Q1=makeQuery(id+"F39.opFillet","BLEND_EDGE",EDGE,{"blendedFrom":[makeQuery(id+"F26.opExtrude","SWEPT_EDGE",EDGE,{"disambiguationData":[OSD([sQuery(id+"F25.wireOp",EDGE,"E31.4"),subQ0])]}),makeQuery(id+"F38.opFillet","BLEND_FACE",FACE,{"disambiguationData":[OSD([subQ0,sQuery(id+"F25.wireOp",EDGE,"E32.right")])]})],"blendedInto":[makeQuery(id+"F38.opFillet","BLEND_FACE",FACE,{"disambiguationData":[OSD([subQ0,sQuery(id+"F25.wireOp",EDGE,"E32.right")])]})]});}
            fillet(context, id + "F40", {"entities" : qUnion([Q0, Q1]), "radius" : 1.02 * mm, "tangentPropagation" : true, "allowEdgeOverflow" : false});
        }
        {
            var Q0;
            Q0=qCreatedBy(id+"F22.planeOp",FACE);
            var sketch = newSketch(context, id + "F41", { "sketchPlane" : qUnion([Q0])});
            skLineSegment(sketch, "E49", {"start": v(-5.09, 3.05) * mm, "end": v(-5.09, 7.23) * mm});
            skLineSegment(sketch, "E50", {"start": v(-7.62, 7.23) * mm, "end": v(-7.62, 5.59) * mm, "construction": true});
            skLineSegment(sketch, "E51", {"start": v(-7.62, -2.41) * mm, "end": v(-7.62, -5.98) * mm});
            skLineSegment(sketch, "E52", {"start": v(-5.09, -5.98) * mm, "end": v(-5.09, -3.05) * mm});
            skLineSegment(sketch, "E53", {"start": v(-7.62, 7.23) * mm, "end": v(-9.54, 7.23) * mm});
            skLineSegment(sketch, "E54", {"start": v(-1.59, 7.23) * mm, "end": v(-5.09, 7.23) * mm});
            skLineSegment(sketch, "E55", {"start": v(-5.09, 6.15) * mm, "end": v(-4.46, 7.23) * mm});
            skLineSegment(sketch, "E56", {"start": v(-5.46, 19.05) * mm, "end": v(-5.46, -6.35) * mm, "construction": true});
            skLineSegment(sketch, "E57", {"start": v(-7.24, -6.35) * mm, "end": v(-7.24, 19.05) * mm, "construction": true});
            skLineSegment(sketch, "E58", {"start": v(-7.24, 6.17) * mm, "end": v(-5.46, 6.17) * mm, "construction": true});
            skLineSegment(sketch, "E59", {"start": v(-6.35, 6.17) * mm, "end": v(-6.35, 8.9) * mm});
            skSolve(sketch);
        }
        {
            var Q0;
            {var subQ3=sQuery(id+"F41.wireOp",EDGE,"E55");Q0=makeQuery(id+"F41.imprint","IMPRINT",FACE,{"disambiguationData":[TD([[makeQuery(id+"F41.imprint","IMPRINT",EDGE,{"derivedFrom":subQ3}),1.0]])]});}
            var Q1;
            Q1=sQuery(id+"F41.wireOp",EDGE,"E59");
            revolve(context, id + "F42", {"operationType" : NewBodyOperationType.REMOVE, "surfaceOperationType" : NewSurfaceOperationType.NEW, "entities" : qUnion([Q0]), "axis" : qUnion([Q1]), "revolveType" : RevolveType.FULL, "oppositeDirection" : true});
        }
        {
            var Q0;
            Q0=makeQuery(id+"F33.boolean.opBoolean","COPY",FACE,{"derivedFrom":makeQuery(id+"F33.opExtrude","CAP_FACE",FACE,{"disambiguationData":[OSD([sQuery(id+"F32.wireOp",EDGE,"E46.0")])],"isStart":true})});
            var sketch = newSketch(context, id + "F43", { "sketchPlane" : qUnion([Q0])});
            skArc(sketch, "E60", {"start": v(8.37, 2.7) * mm, "mid": v(16.03, -1.4) * mm, "end": v(11.11, 5.77) * mm});
            skPoint(sketch, "E61.0", {"position": v(9.54, 7.23) * mm});
            skLineSegment(sketch, "E62", {"start": v(9.54, 7.23) * mm, "end": v(8.37, 2.7) * mm});
            skLineSegment(sketch, "E63.0", {"start": v(11.11, 7.23) * mm, "end": v(9.54, 7.23) * mm});
            skLineSegment(sketch, "E64.0", {"start": v(11.11, -2.8) * mm, "end": v(11.11, -2.6) * mm});
            skLineSegment(sketch, "E65.trimOffspring", {"start": v(11.11, 5.77) * mm, "end": v(11.11, 7.23) * mm});
            skSolve(sketch);
        }
        {
            var Q0;
            Q0=makeQuery(id+"F30.opExtrude","SWEPT_FACE",FACE,{"disambiguationData":[OSD([sQuery(id+"F29.wireOp",EDGE,"E45.left")])]});
            var Q1;
            Q1=sQuery(id+"F43.wireOp",VERTEX,"E60.center");
            cPlane(context, id + "F44", {"entities" : qUnion([Q0, Q1]), "cplaneType" : CPlaneType.PLANE_POINT, "offset" : 25.4 * mm, "width" : 152.4 * mm, "height" : 152.4 * mm});
        }
        {
            var Q0;
            Q0=qCreatedBy(id+"F44.planeOp",FACE);
            var sketch = newSketch(context, id + "F45", { "sketchPlane" : qUnion([Q0])});
            skLineSegment(sketch, "E66", {"start": v(28.78, 1.6) * mm, "end": v(24.35, 1.6) * mm});
            skSolve(sketch);
        }
        {
            var Q0;
            {var subQ0=sQuery(id+"F43.wireOp",EDGE,"E62");Q0=makeQuery(id+"F43.imprint","IMPRINT",FACE,{"disambiguationData":[TD([[makeQuery(id+"F43.imprint","IMPRINT",EDGE,{"derivedFrom":subQ0}),1.0]])]});}
            extrude(context, id + "F46", {"entities" : qUnion([Q0]), "operationType" : NewBodyOperationType.REMOVE, "oppositeDirection" : true, "depth" : 25.4 * mm, "offsetDistance" : 25.4 * mm});
        }
        {
            var Q0;
            Q0=makeQuery(id+"F30.opExtrude","CAP_FACE",FACE,{"disambiguationData":[OSD([sQuery(id+"F29.wireOp",EDGE,"E45.bottom"),sQuery(id+"F29.wireOp",EDGE,"E45.top"),sQuery(id+"F29.wireOp",EDGE,"E45.left"),sQuery(id+"F29.wireOp",EDGE,"E45.right")])],"isStart":false});
            var Q1;
            Q1=sQuery(id+"F45.wireOp",VERTEX,"E66.start");
            cPlane(context, id + "F47", {"entities" : qUnion([Q0, Q1]), "cplaneType" : CPlaneType.PLANE_POINT, "offset" : 25.4 * mm, "width" : 152.4 * mm, "height" : 152.4 * mm});
        }
        {
            var Q0;
            Q0=qCreatedBy(id+"F47.planeOp",FACE);
            var sketch = newSketch(context, id + "F48", { "sketchPlane" : qUnion([Q0])});
            skLineSegment(sketch, "E67", {"start": v(-8.23, -28.78) * mm, "end": v(-6.23, -28.78) * mm});
            skLineSegment(sketch, "E68", {"start": v(-8.23, -30.96) * mm, "end": v(-8.23, -29.59) * mm});
            skLineSegment(sketch, "E69", {"start": v(-7.18, -28.78) * mm, "end": v(-8.23, -29.59) * mm});
            skLineSegment(sketch, "E70", {"start": v(-8.23, -28.78) * mm, "end": v(-8.68, -28.78) * mm});
            skLineSegment(sketch, "E71", {"start": v(-8.68, -28.78) * mm, "end": v(-8.68, -30.96) * mm});
            skLineSegment(sketch, "E72", {"start": v(-8.68, -30.96) * mm, "end": v(-8.23, -30.96) * mm});
            skPoint(sketch, "E73.orphan", {"position": v(-8.23, -28.78) * mm});
            skSolve(sketch);
        }
        {
            var Q0;
            Q0 = qSketchRegion(id + "F48", true);
            var Q1;
            Q1=sQuery(id+"F45.wireOp",EDGE,"E66");
            revolve(context, id + "F49", {"operationType" : NewBodyOperationType.REMOVE, "surfaceOperationType" : NewSurfaceOperationType.NEW, "entities" : qUnion([Q0]), "axis" : qUnion([Q1]), "revolveType" : RevolveType.FULL, "oppositeDirection" : true});
        }
        {
            var Q0;
            Q0=makeQuery(id+"F33.boolean.opBoolean","INTERSECT",EDGE,{"derivedFrom":[makeQuery(id+"F30.opExtrude","CAP_FACE",FACE,{"disambiguationData":[OSD([sQuery(id+"F29.wireOp",EDGE,"E45.bottom"),sQuery(id+"F29.wireOp",EDGE,"E45.top"),sQuery(id+"F29.wireOp",EDGE,"E45.left"),sQuery(id+"F29.wireOp",EDGE,"E45.right")])],"isStart":false}),makeQuery(id+"F33.opExtrude","SWEPT_FACE",FACE,{"disambiguationData":[OSD([sQuery(id+"F32.wireOp",EDGE,"E46.0")])]})]});
            var Q1;
            Q1=makeQuery(id+"F35.boolean.opBoolean","INTERSECT",EDGE,{"disambiguationData":[OD(0.0)],"derivedFrom":[makeQuery(id+"F30.opExtrude","SWEPT_FACE",FACE,{"disambiguationData":[OSD([sQuery(id+"F29.wireOp",EDGE,"E45.right")])]}),makeQuery(id+"F35.opExtrude","SWEPT_FACE",FACE,{"disambiguationData":[OSD([sQuery(id+"F34.wireOp",EDGE,"E47.0")])]})]});
            var Q2;
            Q2=makeQuery(id+"F30.opExtrude","CAP_EDGE",EDGE,{"disambiguationData":[OSD([sQuery(id+"F29.wireOp",EDGE,"E45.right")])],"isStart":false});
            var Q3;
            {var subQ0=sQuery(id+"F29.wireOp",EDGE,"E45.left");Q3=makeQuery(id+"F38.opFillet","BLEND_EDGE",EDGE,{"blendedFrom":[makeQuery(id+"F30.opExtrude","CAP_EDGE",EDGE,{"disambiguationData":[OSD([subQ0])],"isStart":true}),makeQuery(id+"F30.opExtrude","SWEPT_FACE",FACE,{"disambiguationData":[OSD([subQ0])]})],"blendedInto":[makeQuery(id+"F30.opExtrude","SWEPT_FACE",FACE,{"disambiguationData":[OSD([subQ0])]})]});}
            var Q4;
            Q4=makeQuery(id+"F46.boolean.opBoolean","COPY",EDGE,{"derivedFrom":makeQuery(id+"F46.opExtrude","SWEPT_EDGE",EDGE,{"disambiguationData":[OSD([sQuery(id+"F29.wireOp",EDGE,"E45.left"),sQuery(id+"F32.wireOp",EDGE,"E46.0"),sQuery(id+"F43.wireOp",EDGE,"E60"),sQuery(id+"F43.wireOp",EDGE,"E64.0")])]})});
            var Q5;
            Q5=makeQuery(id+"F49.boolean.opBoolean","INTERSECT",EDGE,{"derivedFrom":[makeQuery(id+"F46.boolean.opBoolean","COPY",FACE,{"derivedFrom":makeQuery(id+"F46.opExtrude","SWEPT_FACE",FACE,{"disambiguationData":[OSD([sQuery(id+"F43.wireOp",EDGE,"E62")])]})}),makeQuery(id+"F49.opRevolve","SWEPT_FACE",FACE,{"disambiguationData":[OSD([sQuery(id+"F48.wireOp",EDGE,"E68")])]})]});
            var Q6;
            Q6=makeQuery(id+"F49.boolean.opBoolean","INTERSECT",EDGE,{"derivedFrom":[makeQuery(id+"F46.boolean.opBoolean","COPY",FACE,{"derivedFrom":makeQuery(id+"F46.opExtrude","SWEPT_FACE",FACE,{"disambiguationData":[OSD([sQuery(id+"F43.wireOp",EDGE,"E60")])]})}),makeQuery(id+"F49.opRevolve","SWEPT_FACE",FACE,{"disambiguationData":[OSD([sQuery(id+"F48.wireOp",EDGE,"E68")])]})]});
            var Q7;
            Q7=makeQuery(id+"F28.boolean.opBoolean","COPY",EDGE,{"derivedFrom":makeQuery(id+"F28.opExtrude","SWEPT_EDGE",EDGE,{"disambiguationData":[OSD([sQuery(id+"F25.wireOp",EDGE,"E32.top"),sQuery(id+"F27.wireOp",EDGE,"E40"),sQuery(id+"F27.wireOp",EDGE,"E41")])]})});
            var Q8;
            Q8=makeQuery(id+"F28.boolean.opBoolean","COPY",EDGE,{"derivedFrom":makeQuery(id+"F28.opExtrude","SWEPT_EDGE",EDGE,{"disambiguationData":[OSD([sQuery(id+"F25.wireOp",EDGE,"E32.top"),sQuery(id+"F27.wireOp",EDGE,"E39"),sQuery(id+"F27.wireOp",EDGE,"E41")])]})});
            fillet(context, id + "F50", {"entities" : qUnion([Q0, Q1, Q2, Q3, Q4, Q5, Q6, Q7, Q8]), "radius" : .4 * mm, "tangentPropagation" : true, "allowEdgeOverflow" : false});
        }
        {
            var Q0;
            Q0=makeQuery(id+"F46.boolean.opBoolean","COPY",EDGE,{"derivedFrom":makeQuery(id+"F46.opExtrude","SWEPT_EDGE",EDGE,{"disambiguationData":[OSD([sQuery(id+"F32.wireOp",EDGE,"E46.0"),sQuery(id+"F43.wireOp",EDGE,"E62"),sQuery(id+"F43.wireOp",EDGE,"E63.0")])]})});
            var Q1;
            Q1=makeQuery(id+"F46.boolean.opBoolean","COPY",EDGE,{"derivedFrom":makeQuery(id+"F46.opExtrude","CAP_EDGE",EDGE,{"disambiguationData":[OSD([sQuery(id+"F43.wireOp",EDGE,"E62")])],"isStart":true})});
            var Q2;
            {var subQ0=sQuery(id+"F32.wireOp",EDGE,"E46.0");Q2=makeQuery(id+"F50.opFillet","TWEAK_EDGE",EDGE,{"derivedFrom":[makeQuery(id+"F46.boolean.opBoolean","MERGE",VERTEX,{"derivedFrom":[makeQuery(id+"F33.boolean.opBoolean","INTERSECT",VERTEX,{"derivedFrom":[makeQuery(id+"F30.opExtrude","CAP_FACE",FACE,{"disambiguationData":[OSD([sQuery(id+"F29.wireOp",EDGE,"E45.bottom"),sQuery(id+"F29.wireOp",EDGE,"E45.top"),sQuery(id+"F29.wireOp",EDGE,"E45.left"),sQuery(id+"F29.wireOp",EDGE,"E45.right")])],"isStart":false}),makeQuery(id+"F33.opExtrude","SWEPT_FACE",FACE,{"disambiguationData":[OSD([subQ0])]}),makeQuery(id+"F33.opExtrude","CAP_FACE",FACE,{"disambiguationData":[OSD([subQ0])],"isStart":true})]})],"fromTools":[makeQuery(id+"F46.opExtrude","CAP_VERTEX",VERTEX,{"disambiguationData":[OSD([subQ0,sQuery(id+"F43.wireOp",EDGE,"E62"),sQuery(id+"F43.wireOp",EDGE,"E63.0")])],"isStart":true})]})]});}
            var Q3;
            Q3=makeQuery(id+"F30.opExtrude","CAP_EDGE",EDGE,{"disambiguationData":[OSD([sQuery(id+"F29.wireOp",EDGE,"E45.bottom")])],"isStart":false});
            var Q4;
            Q4=makeQuery(id+"F42.boolean.opBoolean","COPY",EDGE,{"derivedFrom":makeQuery(id+"F42.opRevolve","SWEPT_EDGE",EDGE,{"disambiguationData":[OSD([sQuery(id+"F41.wireOp",EDGE,"E49"),sQuery(id+"F41.wireOp",EDGE,"E55")])]})});
            var Q5;
            Q5=makeQuery(id+"F46.boolean.opBoolean","INTERSECT",EDGE,{"derivedFrom":[makeQuery(id+"F30.boolean.opBoolean","MERGE",FACE,{"derivedFrom":[makeQuery(id+"F26.opExtrude","CAP_FACE",FACE,{"disambiguationData":[OSD([sQuery(id+"F25.wireOp",EDGE,"E31.0"),sQuery(id+"F25.wireOp",EDGE,"E31.1"),sQuery(id+"F25.wireOp",EDGE,"E31.3"),sQuery(id+"F25.wireOp",EDGE,"E31.4"),sQuery(id+"F25.wireOp",EDGE,"E31.5"),sQuery(id+"F25.wireOp",EDGE,"E32.bottom"),sQuery(id+"F25.wireOp",EDGE,"E32.top"),sQuery(id+"F25.wireOp",EDGE,"E32.left"),sQuery(id+"F25.wireOp",EDGE,"E32.right")])],"isStart":true}),makeQuery(id+"F30.opExtrude","SWEPT_FACE",FACE,{"disambiguationData":[OSD([sQuery(id+"F29.wireOp",EDGE,"E45.bottom")])]})]}),makeQuery(id+"F46.opExtrude","SWEPT_FACE",FACE,{"disambiguationData":[OSD([sQuery(id+"F43.wireOp",EDGE,"E60")])]})]});
            var Q6;
            Q6=makeQuery(id+"F28.boolean.opBoolean","COPY",EDGE,{"derivedFrom":makeQuery(id+"F28.opExtrude","CAP_EDGE",EDGE,{"disambiguationData":[OSD([sQuery(id+"F27.wireOp",EDGE,"E42")])],"isStart":true})});
            var Q7;
            {var subQ0=sQuery(id+"F25.wireOp",EDGE,"E32.right");var subQ1=sQuery(id+"F25.wireOp",EDGE,"E32.top");Q7=makeQuery(id+"F28.boolean.opBoolean","SPLIT",EDGE,{"disambiguationData":[TD([makeQuery(id+"F26.opExtrude","SWEPT_FACE",FACE,{"disambiguationData":[OSD([subQ0])]})])],"derivedFrom":makeQuery(id+"F26.opExtrude","CAP_EDGE",EDGE,{"disambiguationData":[OSD([subQ1])],"isStart":false})});}
            var Q8;
            Q8=makeQuery(id+"F28.boolean.opBoolean","COPY",EDGE,{"derivedFrom":makeQuery(id+"F28.opExtrude","SWEPT_EDGE",EDGE,{"disambiguationData":[OSD([sQuery(id+"F25.wireOp",EDGE,"E32.top"),sQuery(id+"F27.wireOp",EDGE,"E43"),sQuery(id+"F27.wireOp",EDGE,"E44")])]})});
            var Q9;
            Q9=makeQuery(id+"F28.boolean.opBoolean","COPY",EDGE,{"derivedFrom":makeQuery(id+"F28.opExtrude","SWEPT_EDGE",EDGE,{"disambiguationData":[OSD([sQuery(id+"F25.wireOp",EDGE,"E32.top"),sQuery(id+"F27.wireOp",EDGE,"E42"),sQuery(id+"F27.wireOp",EDGE,"E43")])]})});
            var Q10;
            {var subQ0=sQuery(id+"F25.wireOp",EDGE,"E32.top");Q10=makeQuery(id+"F28.boolean.opBoolean","SPLIT",EDGE,{"disambiguationData":[TD([makeQuery(id+"F28.opExtrude","SWEPT_FACE",FACE,{"disambiguationData":[OSD([sQuery(id+"F27.wireOp",EDGE,"E40")])]})])],"derivedFrom":makeQuery(id+"F26.opExtrude","CAP_EDGE",EDGE,{"disambiguationData":[OSD([subQ0])],"isStart":false})});}
            var Q11;
            {var subQ0=sQuery(id+"F25.wireOp",EDGE,"E32.left");var subQ1=sQuery(id+"F25.wireOp",EDGE,"E32.top");Q11=makeQuery(id+"F28.boolean.opBoolean","SPLIT",EDGE,{"disambiguationData":[TD([makeQuery(id+"F26.opExtrude","SWEPT_FACE",FACE,{"disambiguationData":[OSD([subQ0])]})])],"derivedFrom":makeQuery(id+"F26.opExtrude","CAP_EDGE",EDGE,{"disambiguationData":[OSD([subQ1])],"isStart":false})});}
            fillet(context, id + "F51", {"entities" : qUnion([Q0, Q1, Q2, Q3, Q4, Q5, Q6, Q7, Q8, Q9, Q10, Q11]), "radius" : .4 * mm, "tangentPropagation" : true, "allowEdgeOverflow" : false});
        }
    });
